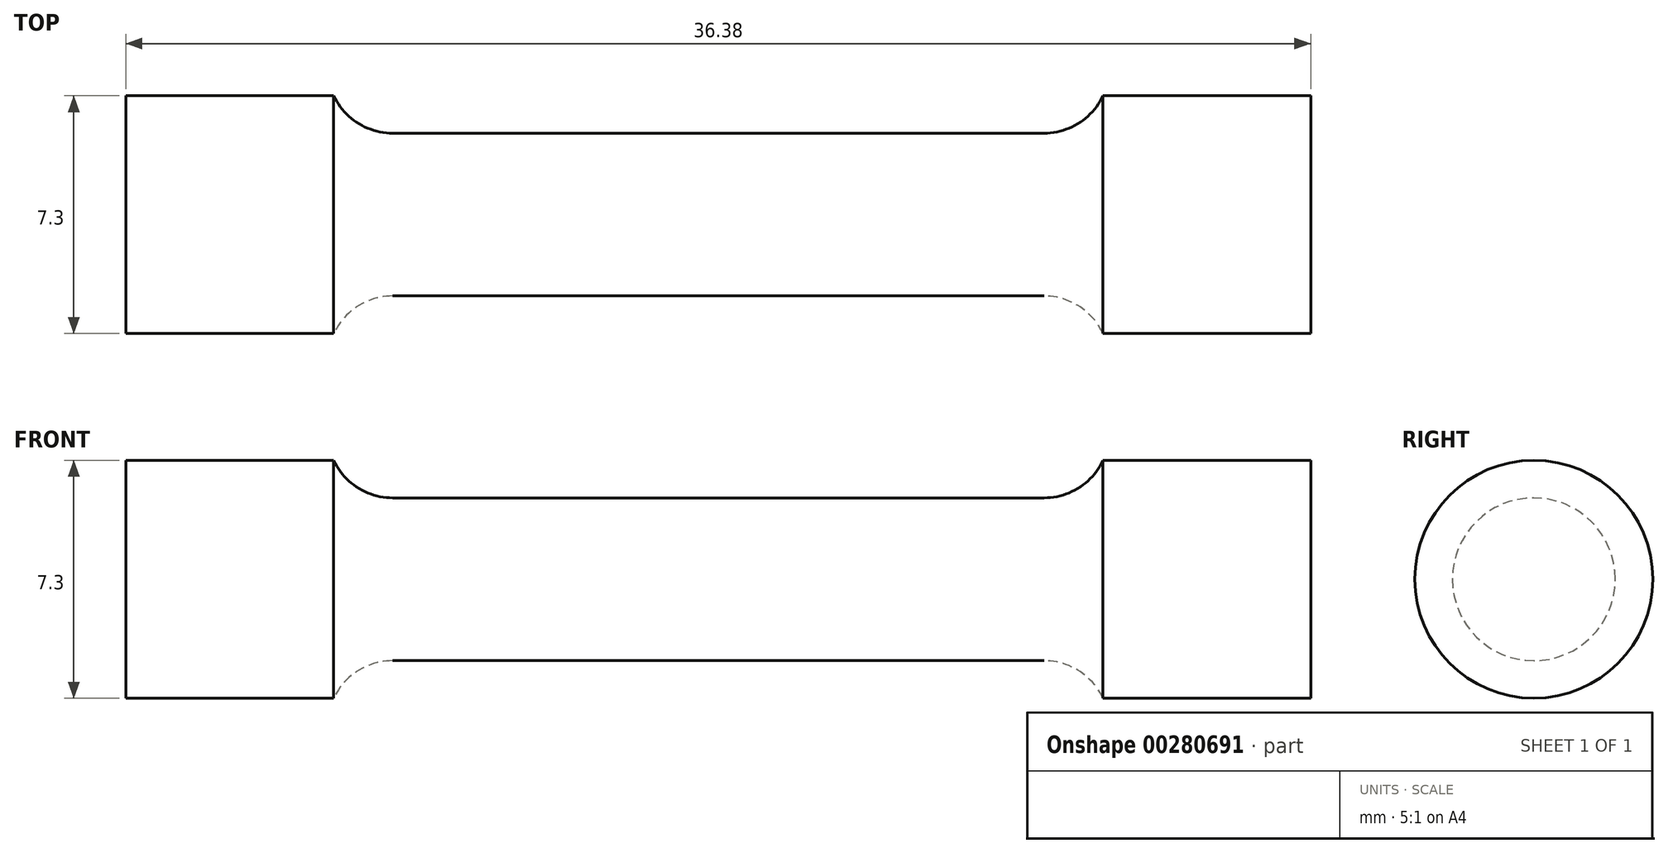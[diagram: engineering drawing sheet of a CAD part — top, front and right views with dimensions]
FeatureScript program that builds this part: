
annotation { "Feature Type Name" : "Feature", "Feature Type Description" : "" }
export const myFeature = defineFeature(function(context is Context, id is Id, definition is map)
    precondition{}
    {
        {
            var Q0;
            Q0=qCreatedBy(makeId("Front.planeOp"),FACE);
            var sketch = newSketch(context, id + "F0", { "sketchPlane" : qUnion([Q0])});
            skLineSegment(sketch, "E0", {"start": v(0, 2.5) * mm, "end": v(10, 2.5) * mm});
            skArc(sketch, "E1", {"start": v(10, 2.5) * mm, "mid": v(11.07, 2.81) * mm, "end": v(11.81, 3.65) * mm});
            skLineSegment(sketch, "E2", {"start": v(11.81, 3.65) * mm, "end": v(18.2, 3.65) * mm});
            skLineSegment(sketch, "E3", {"start": v(18.2, 3.65) * mm, "end": v(18.2, 0) * mm});
            skLineSegment(sketch, "E4.MirrorCS", {"start": v(0, 2.5) * mm, "end": v(-10, 2.5) * mm});
            skArc(sketch, "E5.MirrorCS", {"start": v(-10, 2.5) * mm, "mid": v(-11.07, 2.81) * mm, "end": v(-11.81, 3.65) * mm});
            skLineSegment(sketch, "E6.MirrorCS", {"start": v(-11.81, 3.65) * mm, "end": v(-18.2, 3.65) * mm});
            skLineSegment(sketch, "E7.MirrorCS", {"start": v(-18.2, 3.65) * mm, "end": v(-18.2, 0) * mm});
            skLineSegment(sketch, "E8", {"start": v(-18.2, 0) * mm, "end": v(18.2, 0) * mm});
            skSolve(sketch);
        }
        {
            var Q0;
            Q0 = qSketchRegion(id + "F0", true);
            var Q1;
            Q1=sQuery(id+"F0.wireOp",EDGE,"E8");
            revolve(context, id + "F1", {"entities" : qUnion([Q0]), "axis" : qUnion([Q1]), "revolveType" : RevolveType.FULL});
        }
    });
